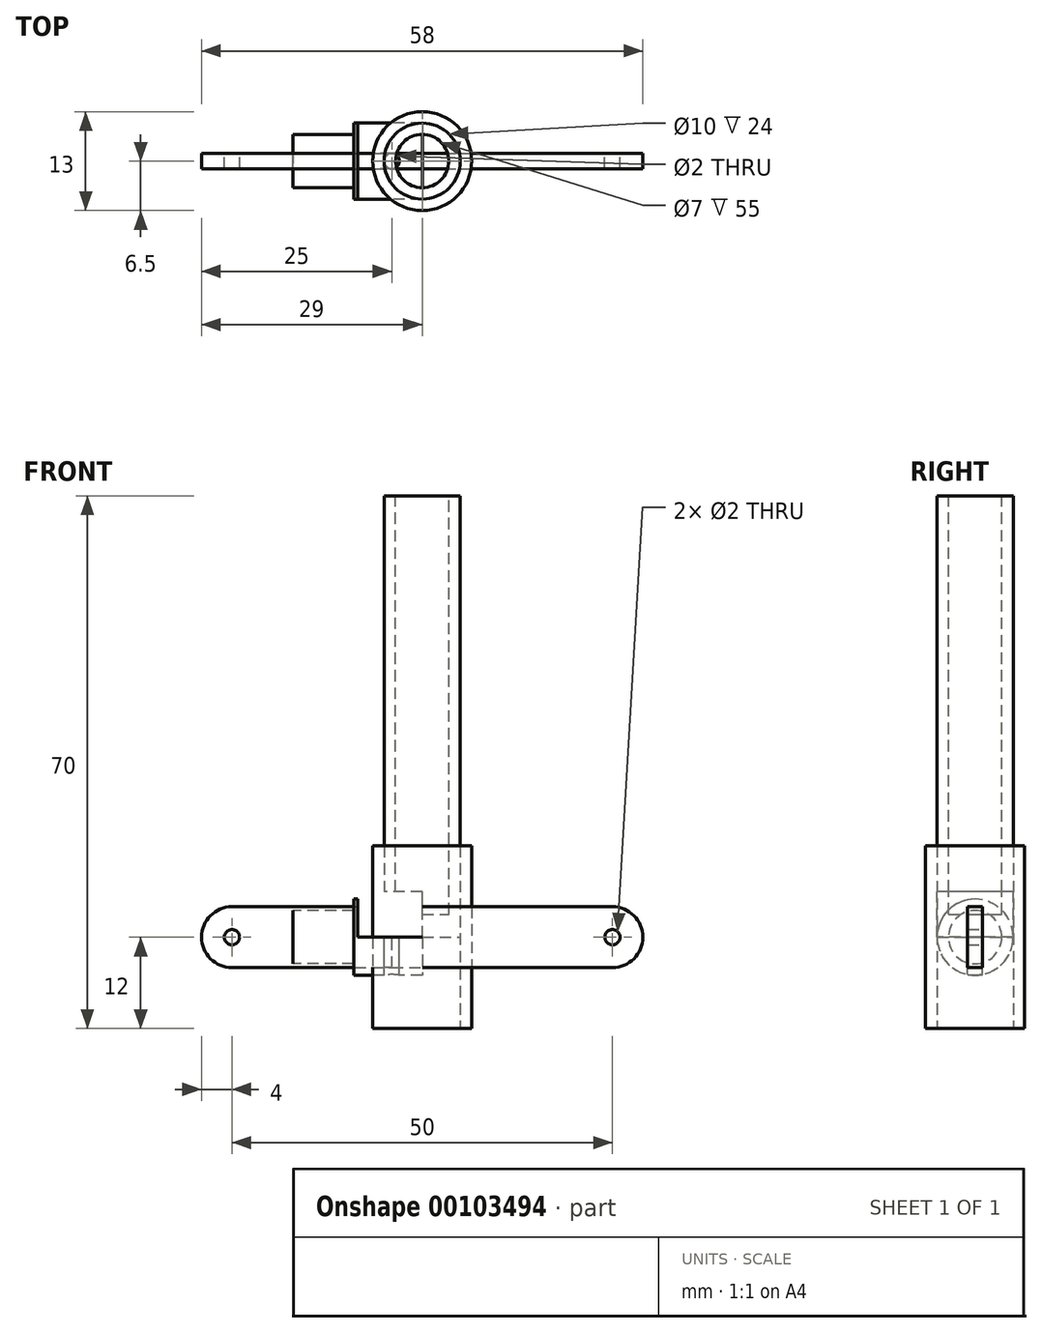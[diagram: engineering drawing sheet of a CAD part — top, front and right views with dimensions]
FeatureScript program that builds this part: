
annotation { "Feature Type Name" : "Feature", "Feature Type Description" : "" }
export const myFeature = defineFeature(function(context is Context, id is Id, definition is map)
    precondition{}
    {
        {
            var Q0;
            Q0=qCreatedBy(makeId("Top.planeOp"),FACE);
            var sketch = newSketch(context, id + "F0", { "sketchPlane" : qUnion([Q0])});
            skCircle(sketch, "E0", {"center": v(0, 0) * mm, "radius": 5 * mm});
            skSolve(sketch);
        }
        {
            var Q0;
            Q0=makeQuery(id+"F0.imprint","IMPRINT",FACE,{"disambiguationData":[TD([[makeQuery(id+"F0.imprint","IMPRINT",EDGE,{"derivedFrom":sQuery(id+"F0.wireOp",EDGE,"E0")}),1.0]])]});
            extrude(context, id + "F1", {"entities" : qUnion([Q0]), "depth" : 58 * mm});
        }
        {
            var Q0;
            Q0=makeQuery(id+"F1.opExtrude","CAP_FACE",FACE,{"disambiguationData":[OSD([sQuery(id+"F0.wireOp",EDGE,"E0")])],"isStart":false});
            var sketch = newSketch(context, id + "F2", { "sketchPlane" : qUnion([Q0])});
            skCircle(sketch, "E1", {"center": v(0, 0) * mm, "radius": 3.5 * mm});
            skSolve(sketch);
        }
        {
            var Q0;
            Q0=makeQuery(id+"F2.imprint","IMPRINT",FACE,{"disambiguationData":[TD([[makeQuery(id+"F2.imprint","IMPRINT",EDGE,{"derivedFrom":sQuery(id+"F2.wireOp",EDGE,"E1")}),1.0]])]});
            extrude(context, id + "F3", {"entities" : qUnion([Q0]), "operationType" : NewBodyOperationType.REMOVE, "oppositeDirection" : true, "depth" : 55 * mm});
        }
        {
            var Q0;
            Q0=qCreatedBy(makeId("Front.planeOp"),FACE);
            var sketch = newSketch(context, id + "F4", { "sketchPlane" : qUnion([Q0])});
            skLineSegment(sketch, "E2", {"start": v(-25, 4) * mm, "end": v(25, 4) * mm});
            skArc(sketch, "E3", {"start": v(25, 4) * mm, "mid": v(29, 0) * mm, "end": v(25, -4) * mm});
            skArc(sketch, "E4", {"start": v(-25, 4) * mm, "mid": v(-29, 0) * mm, "end": v(-25, -4) * mm});
            skLineSegment(sketch, "E5", {"start": v(-25, -4) * mm, "end": v(25, -4) * mm});
            skCircle(sketch, "E6", {"center": v(-25, 0) * mm, "radius": 1 * mm});
            skCircle(sketch, "E7", {"center": v(25, 0) * mm, "radius": 1 * mm});
            skSolve(sketch);
        }
        {
            var Q0;
            Q0=makeQuery(id+"F4.imprint","IMPRINT",FACE,{"disambiguationData":[TD([[makeQuery(id+"F4.imprint","IMPRINT",EDGE,{"derivedFrom":sQuery(id+"F4.wireOp",EDGE,"E2")}),-1.0]])]});
            extrude(context, id + "F5", {"entities" : qUnion([Q0]), "endBound" : BoundingType.SYMMETRIC, "depth" : 2 * mm});
        }
        {
            var Q0;
            Q0=qCreatedBy(makeId("Front.planeOp"),FACE);
            var sketch = newSketch(context, id + "F6", { "sketchPlane" : qUnion([Q0])});
            skLineSegment(sketch, "E8", {"start": v(0, 0) * mm, "end": v(0, 5) * mm});
            skLineSegment(sketch, "E9", {"start": v(0, 5) * mm, "end": v(-9, 5) * mm});
            skLineSegment(sketch, "E10", {"start": v(-9, 5) * mm, "end": v(-9, 3.5) * mm});
            skLineSegment(sketch, "E11", {"start": v(-9, 3.5) * mm, "end": v(-17, 3.5) * mm});
            skLineSegment(sketch, "E12", {"start": v(-17, 3.5) * mm, "end": v(-17, 0) * mm});
            skLineSegment(sketch, "E13", {"start": v(-17, 0) * mm, "end": v(0, 0) * mm});
            skSolve(sketch);
        }
        {
            var Q0;
            Q0=makeQuery(id+"F6.imprint","IMPRINT",FACE,{"disambiguationData":[TD([[makeQuery(id+"F6.imprint","IMPRINT",EDGE,{"derivedFrom":sQuery(id+"F6.wireOp",EDGE,"E8")}),1.0]])]});
            var Q1;
            Q1=sQuery(id+"F6.wireOp",EDGE,"E13");
            revolve(context, id + "F7", {"entities" : qUnion([Q0]), "axis" : qUnion([Q1]), "revolveType" : RevolveType.FULL});
        }
        {
            var Q0;
            Q0=qCreatedBy(makeId("Front.planeOp"),FACE);
            var sketch = newSketch(context, id + "F8", { "sketchPlane" : qUnion([Q0])});
            skLineSegment(sketch, "E14.bottom", {"start": v(0, 0) * mm, "end": v(-8.5, 0) * mm});
            skLineSegment(sketch, "E14.top", {"start": v(0, 6) * mm, "end": v(-8.5, 6) * mm});
            skLineSegment(sketch, "E14.left", {"start": v(0, 0) * mm, "end": v(0, 6) * mm});
            skLineSegment(sketch, "E14.right", {"start": v(-8.5, 0) * mm, "end": v(-8.5, 6) * mm});
            skSolve(sketch);
        }
        {
            var Q0;
            Q0=makeQuery(id+"F8.imprint","IMPRINT",FACE,{"disambiguationData":[TD([[makeQuery(id+"F8.imprint","IMPRINT",EDGE,{"derivedFrom":sQuery(id+"F8.wireOp",EDGE,"E14.bottom")}),-1.0]])]});
            extrude(context, id + "F9", {"entities" : qUnion([Q0]), "operationType" : NewBodyOperationType.REMOVE, "endBound" : BoundingType.SYMMETRIC, "oppositeDirection" : true, "depth" : 10 * mm});
        }
        {
            var Q0;
            Q0=makeQuery(id+"F9.boolean.opBoolean","COPY",FACE,{"derivedFrom":makeQuery(id+"F9.opExtrude","SWEPT_FACE",FACE,{"disambiguationData":[OSD([sQuery(id+"F8.wireOp",EDGE,"E14.bottom")])]})});
            var sketch = newSketch(context, id + "F10", { "sketchPlane" : qUnion([Q0])});
            skCircle(sketch, "E15", {"center": v(-4, 0) * mm, "radius": 1 * mm});
            skSolve(sketch);
        }
        {
            var Q0;
            Q0=makeQuery(id+"F10.imprint","IMPRINT",FACE,{"disambiguationData":[TD([[makeQuery(id+"F10.imprint","IMPRINT",EDGE,{"derivedFrom":sQuery(id+"F10.wireOp",EDGE,"E15")}),1.0]])]});
            extrude(context, id + "F11", {"entities" : qUnion([Q0]), "operationType" : NewBodyOperationType.REMOVE, "endBound" : BoundingType.THROUGH_ALL, "oppositeDirection" : true, "depth" : 25 * mm});
        }
        {
            var Q0;
            Q0=qCreatedBy(makeId("Top.planeOp"),FACE);
            var sketch = newSketch(context, id + "F12", { "sketchPlane" : qUnion([Q0])});
            skCircle(sketch, "E16", {"center": v(0, 0) * mm, "radius": 6.5 * mm});
            skCircle(sketch, "E17", {"center": v(0, 0) * mm, "radius": 5 * mm});
            skSolve(sketch);
        }
        {
            var Q0;
            Q0=makeQuery(id+"F12.imprint","IMPRINT",FACE,{"disambiguationData":[TD([[makeQuery(id+"F12.imprint","IMPRINT",EDGE,{"derivedFrom":sQuery(id+"F12.wireOp",EDGE,"E16")}),1.0]])]});
            extrude(context, id + "F13", {"entities" : qUnion([Q0]), "endBound" : BoundingType.SYMMETRIC, "depth" : 24 * mm});
        }
    });
